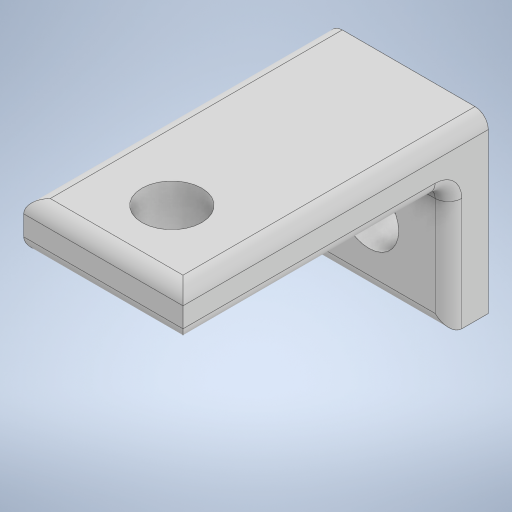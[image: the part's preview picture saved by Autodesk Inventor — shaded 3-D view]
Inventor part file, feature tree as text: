
AUTODESK INVENTOR PART (.ipt)
format: ipt  version: 2024 (Build 280153000, 153)  size: 628,736 bytes
history: native  units: mm
features: sketch x3, extrude x2, hole x1, fillet x1, projected_geometry x1
ambient origin geometry x8: Origin, YZ Plane, XZ Plane, XY Plane, X Axis, Y Axis, Z Axis, Center Point
bodies: Solid1 (feature_tree)
feature tree (8):
  extrude  "Extrusion1"  Depth=5.0mm
  extrude  "Extrusion2"  Depth=6.0mm
  hole  "Hole1"  [1 undecoded]
  fillet  "Fillet1"  Radius=3.0mm
  sketch  "Sketch1"  dims[d0=4.5mm d1=5.0mm]
  sketch  "Sketch2"  dims[d2=6.0mm d3=6.0mm]
  projected_geometry  "Projected Loop1"
  sketch  "Sketch3"  dims[d4=4.5mm d5=3.5mm d6=3.0mm d7=0.0mm d8=3.5mm d9=20.0mm d10=0.0mm d11=4.5mm d12=6.0mm d13=4.0mm d14=2.0mm d15=90.0deg d16=4.0mm d17=20.594885mm d18=1.0mm d19=0.5mm d20=0.872665mm d21=0.5mm d22=0.872665mm]
note: 1 required parameter value undecoded (feature->parameter linkage not recoverable at this tier; creation-order binding heuristic only, values carry confidence <= 0.55)
